# Revit family: PRD_AR_HndDrrs_STRATOSElectronicHandDryer_STR220
name_source: partatom
category: Specialty Equipment
units: mm (PartAtom-declared; Revit-internal decimal feet)

## family parameters
Cut with Voids When Loaded = No
Host = Face
OmniClass Number = 23.40.20.21.14
OmniClass Title = Hand and Hair Dryers
Part Type = Normal
Room Calculation Point = No
Round Connector Dimension = Use Diameter
Shared = No

## types (1)
- STR220
    AirVelocity = Adjustable, 95-115 m/s
    AirVolume = 80.0 m³/h
    AssetType = Fixed
    BIMObjectName = PRD_AR_HndDrrs_STRATOSElectronicHandDryer_STR220
    BlowerOutput = 80m³/h
    Category = Pr_40_70_62_37, Hand dryers
    ConnectionVoltage = 230-240 V, 50-60 Hz
    Default Elevation = 850 mm  [stored 2.78871 ft]
    Description = STRATOS hand dryer for wall mounting, stainless steel, surface satin finished, material thickness 1.5 mm, curved front, with non-contact opto-electronically controlled proximity sensor, adjustable warm air temperature, adjustable sensor range from 10-25 cm, continuous operation protection with automatic switch-off after 60 seconds, adjustable air velocity, cable and plug provided by customer.
    DurationUnit = year
    Features = Stainless steel, surface satin finished
    Finish = satin finished
    GrossWeight = 4.50 kg
    HandDryerMaterial = PRD_AR_StainlessSteel_SatinFinished
    HeatingPower = 500 W
    IP_Code = IPX1
    IfcExportAs = IfcElectricApplianceType
    IfcExportType = HANDDRYER
    InputSupplyVoltageHz = 50 Hz
    InputSupplyVoltageV = 220 V
    IntegralAccessories = cable and plug not included
    LoadClassification = Other
    Manufacturer = KWC Group Management AG
    ManufacturerName = KWC Group Management AG
    ManufacturerURL = www.kwc-professional.com
    Material = Stainless steel
    MaterialCode = 1.4301
    MaterialThickness = 1.50 mm
    Model = STR220
    ModelNumber = 3600008862
    ModelReference = STR220
    MotorPower = 500 W
    NBSDescription = Hand dryers
    NBSReference = 45-35-72/334
    Name = STRATOS Electronic Hand Dryer STR220
    NetWeight = 4.30 kg
    NominalDepth = 130 mm  [stored 0.426509 ft]
    NominalFrequencyRange = 50-60 Hz
    NominalHeight = 267 mm  [stored 0.875984 ft]
    NominalWidth = 156 mm  [stored 0.511811 ft]
    PowerFactor = 1
    ProductInformation = http://pim.kwc.com
    RatedCurrent = 0
    RatedVoltage = 230-240 V
    Size = 156 x 267 x 130 mm
    SoundLevel = 76.20 dB
    TotalPower = 1000 W
    TypeOfFixing = Screw
    TypeOfMounting = Wall mounting
    TypeOfOperation = Sensor operation
    URL = www.kwc-professional.com
    Uniclass2015Code = Pr_40_70_62_37
    Uniclass2015Title = Hand dryers
    Uniclass2015Version = Products v1.10
    Version = 1
    Voltage = 240 V
    WarrantyDurationUnit = year

note: [stored X ft] marks values corroborated as IEEE doubles in the binary element streams (Revit-internal decimal feet)

## geometry (parser evidence)
native form markers: Sweep x6
no freeform markers — native parametric forms only
